# Revit family: RL-1 Rücklaufventil DG 3723
name_source: partatom
category: Rohrzubehör
revit_build: Autodesk Revit 2018 (Build: 20190510_1515(x64)
units: mm (PartAtom-declared; Revit-internal decimal feet)

## family parameters
Arbeitsebenenbasiert = Nein
Beim Laden mit Abzugskörper schneiden = Nein
Bemaßung runder Anschluss = Durchmesser verwenden
Gemeinsam genutzt = Nein
Immer vertikal = Nein
OmniClass-Nummer = 23.65.55.14
OmniClass-Titel = Valves for Liquid Services
Teiletyp = Unterbricht

## types (1)
- RL-1 Rücklaufventil DG 3723
    Anwendungsgebiet = Warmwasserheizungsanlagen
Durch Einbau des Rücklaufventils ist der Heizkörper-Rücklaufanschluß absperrbar.
Dadurch kann bei gleichzeitiger Absperrung des Vorlaufventils der Heizkörper bei unter Druck stehender Anlage demontiert werden.
Es ist dann möglich, Servicearbeiten oder Arbeiten an der Wand hinter dem Heizkörper (Tapezierung, Verﬂ iesung) durchzuführen, ohne die übrige Anlage stillsetzen zu müssen.
Ist eine Voreinstellung des Rücklaufventils oder Füllen und Entleeren von Heizkörper oder Anlage über das Rücklaufventil gefordert, wird der Einbau des Rücklaufventils HERZ-RL-5 empfohlen.
    Ausführungen = Alle Modelle werden in vernickelter Ausführung geliefert und sind Universalmodelle mit Spezialmuffe für Gewinderohr und Klemmsetanschluß.
    Gehäuse = vernickeltes Messing
    H01 = 17 mm
    H03 = 28 mm  [stored 0.0918635 ft]
    H04 = 3.5 mm  [stored 0.0114829 ft]
    H05 = 5.2 mm  [stored 0.0170604 ft]
    Hersteller = HERZ Armaturen Ges.m.b.H.
    LO1 = 7 mm  [stored 0.0229659 ft]
    Max.Betriebsdruck = 1000000.0 Pa
    Max.Betriebstemperatur = 120 °C
    Medium = Heizwasserqualität entsprechend ÖNORM H 5195 bzw. VDI-Richtllinie 2035
    R01 = 10.5 mm  [stored 0.0344488 ft]
    R02 = 11.5 mm  [stored 0.0377297 ft]
    R03 = 28 mm  [stored 0.0918635 ft]
    R04 = 2 mm  [stored 0.00656168 ft]
    R05 = 25 mm  [stored 0.082021 ft]
    R06 = 11 mm  [stored 0.0360892 ft]
    S01 = 10 mm  [stored 0.0328084 ft]
    S03 = 61 mm  [stored 0.200131 ft]
    S04 = 45 mm  [stored 0.147638 ft]
    SCRNCODE = 05;01;02
    SCRNSEQ = ARM;ARM_TYP="ALLF";2
    URL = www.herz-armaturen.at
    W01 = 60.00°

note: [stored X ft] marks values corroborated as IEEE doubles in the binary element streams (Revit-internal decimal feet)
